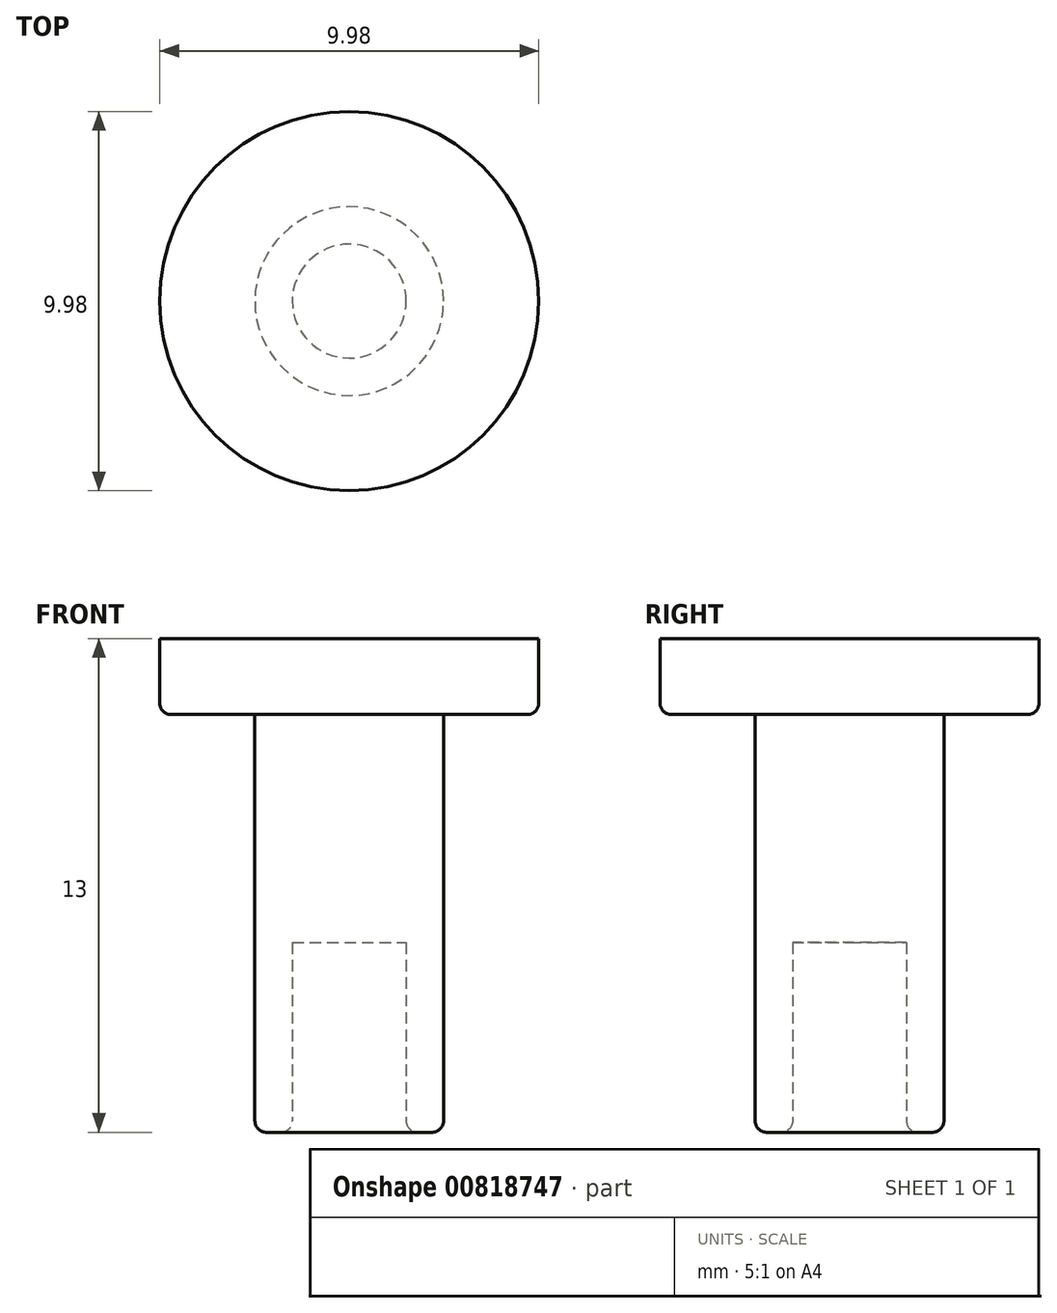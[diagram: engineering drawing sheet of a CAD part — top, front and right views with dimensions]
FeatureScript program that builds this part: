
annotation { "Feature Type Name" : "Feature", "Feature Type Description" : "" }
export const myFeature = defineFeature(function(context is Context, id is Id, definition is map)
    precondition{}
    {
        {
            var Q0;
            Q0=qCreatedBy(makeId("Top.planeOp"),FACE);
            var sketch = newSketch(context, id + "F0", { "sketchPlane" : qUnion([Q0])});
            skCircle(sketch, "E0", {"center": v(0, 0) * mm, "radius": 5 * mm});
            skSolve(sketch);
        }
        {
            var Q0;
            Q0=qSketchRegion(id+"F0",true);
            extrude(context, id + "F1", {"entities" : qUnion([Q0]), "depth" : 2 * mm, "offsetDistance" : 25 * mm});
        }
        {
            var Q0;
            Q0=makeQuery(id+"F1.opExtrude","CAP_FACE",FACE,{"disambiguationData":[OSD([sQuery(id+"F0.wireOp",EDGE,"E0")])],"isStart":true});
            var sketch = newSketch(context, id + "F2", { "sketchPlane" : qUnion([Q0])});
            skCircle(sketch, "E1", {"center": v(0, 0) * mm, "radius": 2.48 * mm});
            skSolve(sketch);
        }
        {
            var Q0;
            Q0=makeQuery(id+"F2.imprint","IMPRINT",FACE,{"disambiguationData":[TD([[makeQuery(id+"F2.imprint","IMPRINT",EDGE,{"derivedFrom":sQuery(id+"F2.wireOp",EDGE,"E1")}),1.0]])]});
            extrude(context, id + "F3", {"entities" : qUnion([Q0]), "operationType" : NewBodyOperationType.ADD, "depth" : 11 * mm, "offsetDistance" : 25 * mm});
        }
        {
            var Q0;
            Q0=makeQuery(id+"F3.opExtrude","CAP_FACE",FACE,{"disambiguationData":[OSD([sQuery(id+"F2.wireOp",EDGE,"E1")])],"isStart":false});
            var sketch = newSketch(context, id + "F4", { "sketchPlane" : qUnion([Q0])});
            skCircle(sketch, "E2", {"center": v(0, 0) * mm, "radius": 1.5 * mm});
            skSolve(sketch);
        }
        {
            var Q0;
            Q0=makeQuery(id+"F4.imprint","IMPRINT",FACE,{"disambiguationData":[TD([[makeQuery(id+"F4.imprint","IMPRINT",EDGE,{"derivedFrom":sQuery(id+"F4.wireOp",EDGE,"E2")}),1.0]])]});
            extrude(context, id + "F5", {"entities" : qUnion([Q0]), "operationType" : NewBodyOperationType.REMOVE, "oppositeDirection" : true, "depth" : 5 * mm, "offsetDistance" : 25 * mm});
        }
        {
            var Q0;
            Q0=makeQuery(id+"F3.opExtrude","CAP_FACE",FACE,{"disambiguationData":[OSD([sQuery(id+"F2.wireOp",EDGE,"E1")])],"isStart":false});
            var Q1;
            Q1=makeQuery(id+"F1.opExtrude","CAP_EDGE",EDGE,{"disambiguationData":[OSD([sQuery(id+"F0.wireOp",EDGE,"E0")])],"isStart":true});
            fillet(context, id + "F6", {"entities" : qUnion([Q0, Q1]), "radius" : .3 * mm, "tangentPropagation" : true, "allowEdgeOverflow" : false});
        }
    });
